# Revit family: Contour HD24
name_source: partatom
category: Lighting Fixtures
revit_build: Autodesk Revit LT 2015 (Build: 20140606_1530(x64)
units: mm (PartAtom-declared; Revit-internal decimal feet)

## types (1)
- Contour HD24/10W/927/1metre
    BIMObjectName = Contour HD24
    BallastCELMAEnergyEfficiencyIndex = See driver specification
    Beam Width = Extra Wide
    CableLength = 0 mm  [stored 0 ft]
    CodePerformance = LICO24HD1
    Color Filter = 16777215
    Description = Extra warm white strip
    Dimming Lamp Color Temperature Shift = <None>
    DurationUnit = year
    Efficacy = 44.5 lm/W
    Emit from Line Length = 610 mm
    ExpectedLife = Lifetime L70/B10 >50,000 hrs
    Finish = 1 metre
    ForwardVoltage = 24V DC
    IngressProtection = IP20
    InsulationStandardClass = Class III
    Keynote = Technical data figures are for guidance only and are subject to ±5% tolerance
    LampColourRendering = ≥90 Ra
    LampColourTemperature = 2700K
    LampLumens = 445 lm
    LampType = LED
    LuminaireLumens = 445 lm
    Manufacturer = John Cullen Lighting Ltd
    ManufacturerName = John Cullen Lighting Ltd
    ManufacturerURL = www.johncullenlighting.co.uk
    MaxAmbientTemperature = 45.00°
    Model = Contour HD24
    ModelNumber = LICO24HD1
    NBSDescription = General purpose luminaires are described by characteristics such as standards, photometric performance and supply circuit conductor connections.
An example use may be within a hard wired general lighting system.
    Name = Contour HD24
    NominalHeight = 2 mm  [stored 0.00656168 ft]
    NominalLength = 1 mm  [stored 0.00328084 ft]
    NominalWidth = 8 mm  [stored 0.0262467 ft]
    Photometric Web File = ContourHD24-24.IES
    ProductInformation = http://www.johncullenlighting.co.uk
    Shape = Linear
    Size = 8x2x1000
    Tilt Angle = 90.00°
    URL = http://www.johncullenlighting.co.uk
    Uniclass2 = Pr_70_70_48_85 Surface luminaires
    Version = 1
    WarrantyDescription = Refer to John Cullen Lighting Ltd - Terms and Conditions document
    WarrantyDurationLabor = www.johncullenlighting.co.uk/terms_and_conditions/
    WarrantyDurationParts = www.johncullenlighting.co.uk/terms_and_conditions/
    WarrantyDurationUnit = www.johncullenlighting.co.uk/terms_and_conditions/
    WarrantyGuarantorLabor = www.johncullenlighting.co.uk/terms_and_conditions/
    WarrantyGuarantorParts = www.johncullenlighting.co.uk/terms_and_conditions/
    Wattage = 10 W
    Weight = 0

note: [stored X ft] marks values corroborated as IEEE doubles in the binary element streams (Revit-internal decimal feet)

## geometry (parser evidence)
native form markers: Sweep x3
no freeform markers — native parametric forms only
